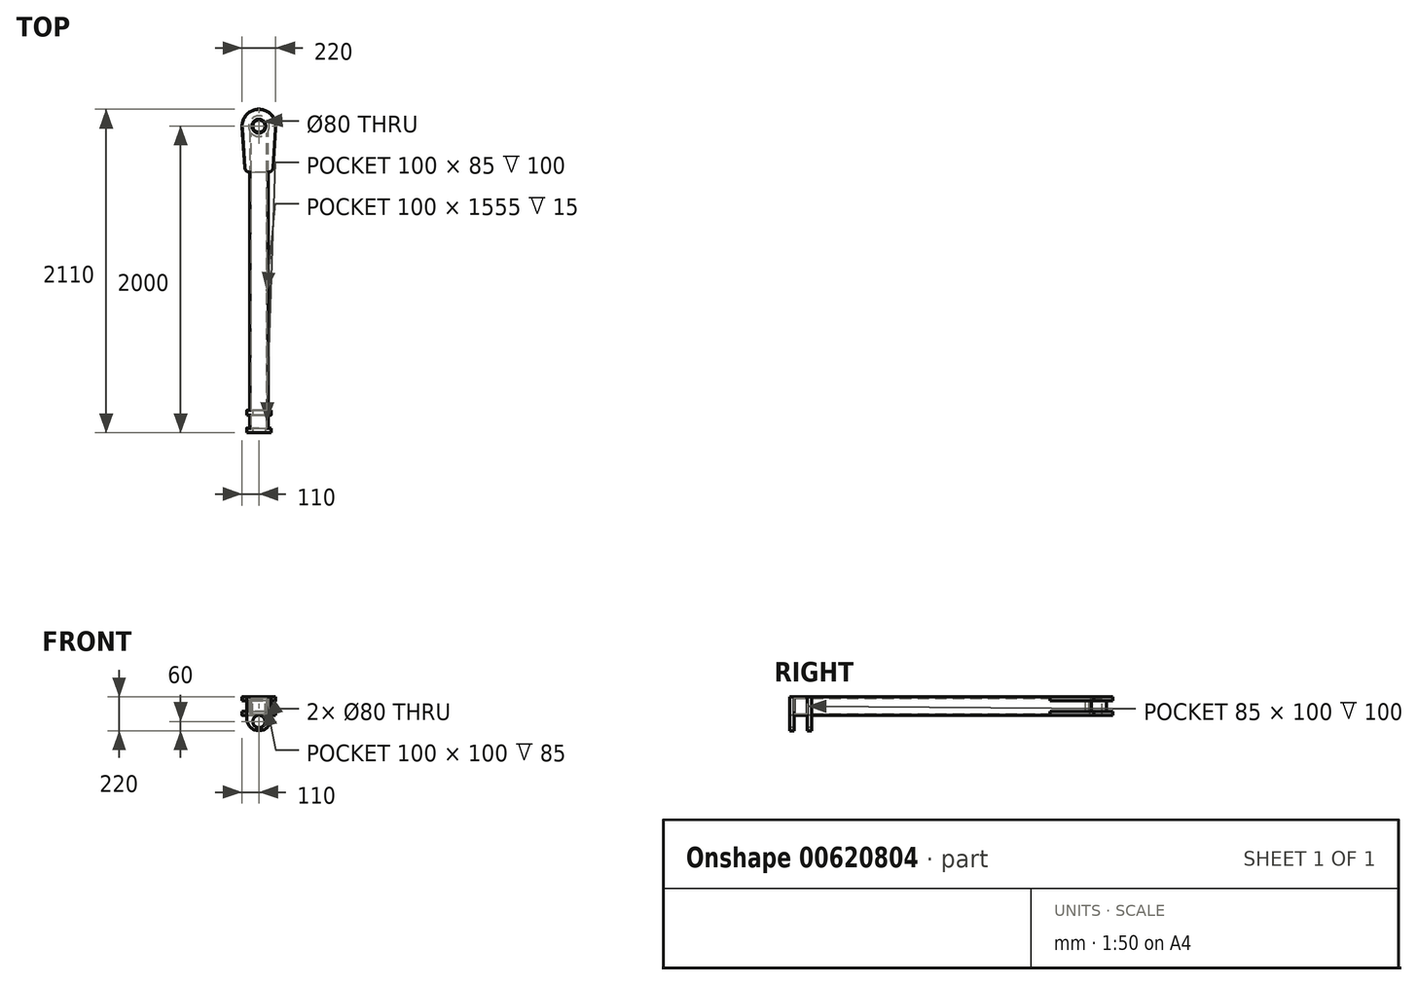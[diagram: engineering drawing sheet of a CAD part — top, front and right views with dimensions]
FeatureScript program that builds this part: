
annotation { "Feature Type Name" : "Feature", "Feature Type Description" : "" }
export const myFeature = defineFeature(function(context is Context, id is Id, definition is map)
    precondition{}
    {
        {
            var Q0;
            Q0=qCreatedBy(makeId("Front.planeOp"),FACE);
            var sketch = newSketch(context, id + "F0", { "sketchPlane" : qUnion([Q0])});
            skLineSegment(sketch, "E0.bottom", {"start": v(-60, 60) * mm, "end": v(60, 60) * mm});
            skLineSegment(sketch, "E0.top", {"start": v(-60, -60) * mm, "end": v(60, -60) * mm});
            skLineSegment(sketch, "E0.left", {"start": v(-60, 60) * mm, "end": v(-60, -60) * mm});
            skLineSegment(sketch, "E0.right", {"start": v(60, 60) * mm, "end": v(60, -60) * mm});
            skPoint(sketch, "E0.middle", {"position": v(0, 0) * mm});
            skLineSegment(sketch, "E1.bottom", {"start": v(-50, 50) * mm, "end": v(50, 50) * mm});
            skLineSegment(sketch, "E1.top", {"start": v(-50, -50) * mm, "end": v(50, -50) * mm});
            skLineSegment(sketch, "E1.left", {"start": v(-50, 50) * mm, "end": v(-50, -50) * mm});
            skLineSegment(sketch, "E1.right", {"start": v(50, 50) * mm, "end": v(50, -50) * mm});
            skSolve(sketch);
        }
        {
            var Q0;
            Q0 = qSketchRegion(id + "F0", true);
            extrude(context, id + "F1", {"entities" : qUnion([Q0]), "endBound" : BoundingType.SYMMETRIC, "depth" : 2000 * mm, "offsetDistance" : 25 * mm});
        }
        {
            var Q0;
            Q0=makeQuery(id+"F1.opExtrude","SWEPT_FACE",FACE,{"disambiguationData":[OSD([sQuery(id+"F0.wireOp",EDGE,"E0.bottom")])]});
            var sketch = newSketch(context, id + "F2", { "sketchPlane" : qUnion([Q0])});
            skCircle(sketch, "E2", {"center": v(0, 1000) * mm, "radius": 67.5 * mm});
            skSolve(sketch);
        }
        {
            var Q0;
            Q0 = qSketchRegion(id + "F2", true);
            extrude(context, id + "F3", {"entities" : qUnion([Q0]), "operationType" : NewBodyOperationType.ADD, "oppositeDirection" : true, "depth" : 120 * mm, "offsetDistance" : 25 * mm});
        }
        {
            var Q0;
            Q0=makeQuery(id+"F3.boolean.opBoolean","MERGE",FACE,{"derivedFrom":[makeQuery(id+"F1.opExtrude","SWEPT_FACE",FACE,{"disambiguationData":[OSD([sQuery(id+"F0.wireOp",EDGE,"E0.bottom")])]}),makeQuery(id+"F3.opExtrude","CAP_FACE",FACE,{"disambiguationData":[OSD([sQuery(id+"F2.wireOp",EDGE,"E2")])],"isStart":true})]});
            var sketch = newSketch(context, id + "F4", { "sketchPlane" : qUnion([Q0])});
            skCircle(sketch, "E3", {"center": v(0, 1000) * mm, "radius": 40 * mm});
            skSolve(sketch);
        }
        {
            var Q0;
            Q0 = qSketchRegion(id + "F4", true);
            extrude(context, id + "F5", {"entities" : qUnion([Q0]), "operationType" : NewBodyOperationType.REMOVE, "oppositeDirection" : true, "depth" : 120 * mm, "offsetDistance" : 25 * mm});
        }
        {
            var Q0;
            Q0=makeQuery(id+"F3.boolean.opBoolean","MERGE",FACE,{"derivedFrom":[makeQuery(id+"F1.opExtrude","SWEPT_FACE",FACE,{"disambiguationData":[OSD([sQuery(id+"F0.wireOp",EDGE,"E0.bottom")])]}),makeQuery(id+"F3.opExtrude","CAP_FACE",FACE,{"disambiguationData":[OSD([sQuery(id+"F2.wireOp",EDGE,"E2")])],"isStart":true})]});
            var sketch = newSketch(context, id + "F6", { "sketchPlane" : qUnion([Q0])});
            skCircle(sketch, "E4", {"center": v(0, 1000) * mm, "radius": 110 * mm});
            skLineSegment(sketch, "E5", {"start": v(-110, 1000) * mm, "end": v(-90, 700) * mm});
            skLineSegment(sketch, "E6", {"start": v(-90, 700) * mm, "end": v(90, 700) * mm});
            skLineSegment(sketch, "E7", {"start": v(90, 700) * mm, "end": v(110, 1000) * mm});
            skSolve(sketch);
        }
        {
            var Q0;
            Q0 = qSketchRegion(id + "F6", true);
            extrude(context, id + "F7", {"entities" : qUnion([Q0]), "operationType" : NewBodyOperationType.ADD, "oppositeDirection" : true, "depth" : 25 * mm, "offsetDistance" : 25 * mm});
        }
        {
            var Q0;
            Q0=makeQuery(id+"F3.boolean.opBoolean","MERGE",FACE,{"derivedFrom":[makeQuery(id+"F1.opExtrude","SWEPT_FACE",FACE,{"disambiguationData":[OSD([sQuery(id+"F0.wireOp",EDGE,"E0.top")])]}),makeQuery(id+"F3.opExtrude","CAP_FACE",FACE,{"disambiguationData":[OSD([sQuery(id+"F2.wireOp",EDGE,"E2")])],"isStart":false})]});
            var sketch = newSketch(context, id + "F8", { "sketchPlane" : qUnion([Q0])});
            skCircle(sketch, "E8", {"center": v(0, -1000) * mm, "radius": 110 * mm});
            skLineSegment(sketch, "E9", {"start": v(110, -1000) * mm, "end": v(90, -700) * mm});
            skLineSegment(sketch, "E10", {"start": v(90, -700) * mm, "end": v(-90, -700) * mm});
            skLineSegment(sketch, "E11", {"start": v(-90, -700) * mm, "end": v(-110.25, -1000) * mm});
            skSolve(sketch);
        }
        {
            var Q0;
            Q0 = qSketchRegion(id + "F8", true);
            extrude(context, id + "F9", {"entities" : qUnion([Q0]), "operationType" : NewBodyOperationType.ADD, "oppositeDirection" : true, "depth" : 25 * mm, "offsetDistance" : 25 * mm});
        }
        {
            var Q0;
            Q0=makeQuery(id+"F9.boolean.opBoolean","MERGE",FACE,{"derivedFrom":[makeQuery(id+"F3.boolean.opBoolean","MERGE",FACE,{"derivedFrom":[makeQuery(id+"F1.opExtrude","SWEPT_FACE",FACE,{"disambiguationData":[OSD([sQuery(id+"F0.wireOp",EDGE,"E0.top")])]}),makeQuery(id+"F3.opExtrude","CAP_FACE",FACE,{"disambiguationData":[OSD([sQuery(id+"F2.wireOp",EDGE,"E2")])],"isStart":false})]}),makeQuery(id+"F9.opExtrude","CAP_FACE",FACE,{"disambiguationData":[OSD([sQuery(id+"F8.wireOp",EDGE,"E8"),sQuery(id+"F8.wireOp",EDGE,"E9"),sQuery(id+"F8.wireOp",EDGE,"E10"),sQuery(id+"F8.wireOp",EDGE,"E11")])],"isStart":true})]});
            var sketch = newSketch(context, id + "F10", { "sketchPlane" : qUnion([Q0])});
            skCircle(sketch, "E12", {"center": v(0, -1000) * mm, "radius": 40 * mm});
            skSolve(sketch);
        }
        {
            var Q0;
            Q0 = qSketchRegion(id + "F10", true);
            extrude(context, id + "F11", {"entities" : qUnion([Q0]), "operationType" : NewBodyOperationType.REMOVE, "oppositeDirection" : true, "depth" : 160 * mm, "offsetDistance" : 25 * mm});
        }
        {
            var Q0;
            Q0=makeQuery(id+"F1.opExtrude","SWEPT_FACE",FACE,{"disambiguationData":[OSD([sQuery(id+"F0.wireOp",EDGE,"E0.right")])]});
            var sketch = newSketch(context, id + "F12", { "sketchPlane" : qUnion([Q0])});
            skLineSegment(sketch, "E13.bottom", {"start": v(-885, 60) * mm, "end": v(-855, 60) * mm});
            skLineSegment(sketch, "E13.top", {"start": v(-885, -160) * mm, "end": v(-855, -160) * mm});
            skLineSegment(sketch, "E13.left", {"start": v(-885, 60) * mm, "end": v(-885, -160) * mm});
            skLineSegment(sketch, "E13.right", {"start": v(-855, 60) * mm, "end": v(-855, -160) * mm});
            skSolve(sketch);
        }
        {
            var Q0;
            Q0 = qSketchRegion(id + "F12", true);
            extrude(context, id + "F13", {"entities" : qUnion([Q0]), "operationType" : NewBodyOperationType.ADD, "oppositeDirection" : true, "depth" : 140 * mm, "offsetDistance" : 25 * mm});
        }
        {
            var Q0;
            Q0=makeQuery(id+"F13.boolean.opBoolean","MERGE",FACE,{"derivedFrom":[makeQuery(id+"F1.opExtrude","SWEPT_FACE",FACE,{"disambiguationData":[OSD([sQuery(id+"F0.wireOp",EDGE,"E0.right")])]}),makeQuery(id+"F13.opExtrude","CAP_FACE",FACE,{"disambiguationData":[OSD([sQuery(id+"F12.wireOp",EDGE,"E13.bottom"),sQuery(id+"F12.wireOp",EDGE,"E13.top"),sQuery(id+"F12.wireOp",EDGE,"E13.left"),sQuery(id+"F12.wireOp",EDGE,"E13.right")])],"isStart":true})]});
            var sketch = newSketch(context, id + "F14", { "sketchPlane" : qUnion([Q0])});
            skLineSegment(sketch, "E14.bottom", {"start": v(-885, -160) * mm, "end": v(-855, -160) * mm});
            skLineSegment(sketch, "E14.top", {"start": v(-885, 60) * mm, "end": v(-855, 60) * mm});
            skLineSegment(sketch, "E14.left", {"start": v(-885, -160) * mm, "end": v(-885, 60) * mm});
            skLineSegment(sketch, "E14.right", {"start": v(-855, -160) * mm, "end": v(-855, 60) * mm});
            skSolve(sketch);
        }
        {
            var Q0;
            Q0 = qSketchRegion(id + "F14", true);
            extrude(context, id + "F15", {"entities" : qUnion([Q0]), "operationType" : NewBodyOperationType.ADD, "depth" : 20 * mm, "offsetDistance" : 25 * mm});
        }
        {
            var Q0;
            {var subQ0=sQuery(id+"F12.wireOp",EDGE,"E13.left");var subQ1=sQuery(id+"F12.wireOp",EDGE,"E13.bottom");var subQ5=sQuery(id+"F0.wireOp",EDGE,"E0.right");Q0=makeQuery(id+"F15.boolean.opBoolean","SPLIT",FACE,{"disambiguationData":[TD([makeQuery(id+"F13.opExtrude","SWEPT_FACE",FACE,{"disambiguationData":[OSD([subQ0])]})])],"derivedFrom":makeQuery(id+"F13.boolean.opBoolean","MERGE",FACE,{"derivedFrom":[makeQuery(id+"F1.opExtrude","SWEPT_FACE",FACE,{"disambiguationData":[OSD([subQ5])]}),makeQuery(id+"F13.opExtrude","CAP_FACE",FACE,{"disambiguationData":[OSD([subQ1,sQuery(id+"F12.wireOp",EDGE,"E13.top"),subQ0,sQuery(id+"F12.wireOp",EDGE,"E13.right")])],"isStart":true})]})});}
            var sketch = newSketch(context, id + "F16", { "sketchPlane" : qUnion([Q0])});
            skLineSegment(sketch, "E15.bottom", {"start": v(-1000, 60) * mm, "end": v(-970, 60) * mm});
            skLineSegment(sketch, "E15.top", {"start": v(-1000, -160) * mm, "end": v(-970, -160) * mm});
            skLineSegment(sketch, "E15.left", {"start": v(-1000, 60) * mm, "end": v(-1000, -160) * mm});
            skLineSegment(sketch, "E15.right", {"start": v(-970, 60) * mm, "end": v(-970, -160) * mm});
            skSolve(sketch);
        }
        {
            var Q0;
            Q0 = qSketchRegion(id + "F16", true);
            extrude(context, id + "F17", {"entities" : qUnion([Q0]), "operationType" : NewBodyOperationType.ADD, "oppositeDirection" : true, "depth" : 140 * mm, "offsetDistance" : 25 * mm});
        }
        {
            var Q0;
            {var subQ0=sQuery(id+"F12.wireOp",EDGE,"E13.left");var subQ1=sQuery(id+"F12.wireOp",EDGE,"E13.bottom");var subQ5=sQuery(id+"F0.wireOp",EDGE,"E0.right");Q0=makeQuery(id+"F17.boolean.opBoolean","MERGE",FACE,{"derivedFrom":[makeQuery(id+"F15.boolean.opBoolean","SPLIT",FACE,{"disambiguationData":[TD([makeQuery(id+"F13.opExtrude","SWEPT_FACE",FACE,{"disambiguationData":[OSD([subQ0])]})])],"derivedFrom":makeQuery(id+"F13.boolean.opBoolean","MERGE",FACE,{"derivedFrom":[makeQuery(id+"F1.opExtrude","SWEPT_FACE",FACE,{"disambiguationData":[OSD([subQ5])]}),makeQuery(id+"F13.opExtrude","CAP_FACE",FACE,{"disambiguationData":[OSD([subQ1,sQuery(id+"F12.wireOp",EDGE,"E13.top"),subQ0,sQuery(id+"F12.wireOp",EDGE,"E13.right")])],"isStart":true})]})}),makeQuery(id+"F17.opExtrude","CAP_FACE",FACE,{"disambiguationData":[OSD([sQuery(id+"F16.wireOp",EDGE,"E15.bottom"),sQuery(id+"F16.wireOp",EDGE,"E15.top"),sQuery(id+"F16.wireOp",EDGE,"E15.left"),sQuery(id+"F16.wireOp",EDGE,"E15.right")])],"isStart":true})]});}
            var sketch = newSketch(context, id + "F18", { "sketchPlane" : qUnion([Q0])});
            skLineSegment(sketch, "E16.bottom", {"start": v(-1000, -160) * mm, "end": v(-970, -160) * mm});
            skLineSegment(sketch, "E16.top", {"start": v(-1000, 60) * mm, "end": v(-970, 60) * mm});
            skLineSegment(sketch, "E16.left", {"start": v(-1000, -160) * mm, "end": v(-1000, 60) * mm});
            skLineSegment(sketch, "E16.right", {"start": v(-970, -160) * mm, "end": v(-970, 60) * mm});
            skSolve(sketch);
        }
        {
            var Q0;
            Q0 = qSketchRegion(id + "F18", true);
            extrude(context, id + "F19", {"entities" : qUnion([Q0]), "operationType" : NewBodyOperationType.ADD, "depth" : 20 * mm, "offsetDistance" : 25 * mm});
        }
        {
            var Q0;
            Q0=makeQuery(id+"F19.boolean.opBoolean","MERGE",FACE,{"derivedFrom":[makeQuery(id+"F17.boolean.opBoolean","MERGE",FACE,{"derivedFrom":[makeQuery(id+"F1.opExtrude","CAP_FACE",FACE,{"disambiguationData":[OSD([sQuery(id+"F0.wireOp",EDGE,"E0.bottom"),sQuery(id+"F0.wireOp",EDGE,"E0.top"),sQuery(id+"F0.wireOp",EDGE,"E0.left"),sQuery(id+"F0.wireOp",EDGE,"E0.right"),sQuery(id+"F0.wireOp",EDGE,"E1.bottom"),sQuery(id+"F0.wireOp",EDGE,"E1.top"),sQuery(id+"F0.wireOp",EDGE,"E1.left"),sQuery(id+"F0.wireOp",EDGE,"E1.right")])],"isStart":false}),makeQuery(id+"F17.opExtrude","SWEPT_FACE",FACE,{"disambiguationData":[OSD([sQuery(id+"F16.wireOp",EDGE,"E15.left")])]})]}),makeQuery(id+"F19.opExtrude","SWEPT_FACE",FACE,{"disambiguationData":[OSD([sQuery(id+"F18.wireOp",EDGE,"E16.left")])]})]});
            var sketch = newSketch(context, id + "F20", { "sketchPlane" : qUnion([Q0])});
            skCircle(sketch, "E17", {"center": v(0, -100) * mm, "radius": 40 * mm});
            skPoint(sketch, "E17.centerSnap0", {"position": v(0, -160) * mm});
            skSolve(sketch);
        }
        {
            var Q0;
            Q0 = qSketchRegion(id + "F20", true);
            extrude(context, id + "F21", {"entities" : qUnion([Q0]), "operationType" : NewBodyOperationType.REMOVE, "oppositeDirection" : true, "depth" : 145 * mm, "offsetDistance" : 25 * mm});
        }
        {
            var Q0;
            {var subQ0=sQuery(id+"F6.wireOp",EDGE,"E6");var subQ1=sQuery(id+"F0.wireOp",EDGE,"E0.right");var subQ4=sQuery(id+"F0.wireOp",EDGE,"E0.bottom");Q0=makeQuery(id+"F15.boolean.opBoolean","SPLIT",EDGE,{"disambiguationData":[TD([makeQuery(id+"F7.opExtrude","SWEPT_FACE",FACE,{"disambiguationData":[OSD([subQ0])]})])],"derivedFrom":makeQuery(id+"F1.opExtrude","SWEPT_EDGE",EDGE,{"disambiguationData":[OSD([subQ4,subQ1])]})});}
            var Q1;
            {var subQ0=sQuery(id+"F8.wireOp",EDGE,"E10");var subQ1=sQuery(id+"F0.wireOp",EDGE,"E0.top");var subQ2=sQuery(id+"F0.wireOp",EDGE,"E0.right");Q1=makeQuery(id+"F13.boolean.opBoolean","SPLIT",EDGE,{"disambiguationData":[TD([makeQuery(id+"F9.opExtrude","SWEPT_FACE",FACE,{"disambiguationData":[OSD([subQ0])]})])],"derivedFrom":makeQuery(id+"F1.opExtrude","SWEPT_EDGE",EDGE,{"disambiguationData":[OSD([subQ1,subQ2])]})});}
            var Q2;
            {var subQ0=sQuery(id+"F0.wireOp",EDGE,"E0.top");var subQ1=sQuery(id+"F0.wireOp",EDGE,"E0.right");var subQ2=sQuery(id+"F12.wireOp",EDGE,"E13.left");Q2=makeQuery(id+"F13.boolean.opBoolean","SPLIT",EDGE,{"disambiguationData":[TD([makeQuery(id+"F13.opExtrude","SWEPT_FACE",FACE,{"disambiguationData":[OSD([subQ2])]})])],"derivedFrom":makeQuery(id+"F1.opExtrude","SWEPT_EDGE",EDGE,{"disambiguationData":[OSD([subQ0,subQ1])]})});}
            var Q3;
            {var subQ0=sQuery(id+"F0.wireOp",EDGE,"E0.right");var subQ1=sQuery(id+"F0.wireOp",EDGE,"E0.bottom");var subQ2=sQuery(id+"F12.wireOp",EDGE,"E13.left");Q3=makeQuery(id+"F15.boolean.opBoolean","SPLIT",EDGE,{"disambiguationData":[TD([makeQuery(id+"F13.opExtrude","SWEPT_FACE",FACE,{"disambiguationData":[OSD([subQ2])]})])],"derivedFrom":makeQuery(id+"F1.opExtrude","SWEPT_EDGE",EDGE,{"disambiguationData":[OSD([subQ1,subQ0])]})});}
            var Q4;
            {var subQ0=sQuery(id+"F6.wireOp",EDGE,"E6");var subQ1=sQuery(id+"F0.wireOp",EDGE,"E0.left");var subQ2=sQuery(id+"F0.wireOp",EDGE,"E0.bottom");Q4=makeQuery(id+"F13.boolean.opBoolean","SPLIT",EDGE,{"disambiguationData":[TD([makeQuery(id+"F7.opExtrude","SWEPT_FACE",FACE,{"disambiguationData":[OSD([subQ0])]})])],"derivedFrom":makeQuery(id+"F1.opExtrude","SWEPT_EDGE",EDGE,{"disambiguationData":[OSD([subQ2,subQ1])]})});}
            var Q5;
            {var subQ0=sQuery(id+"F0.wireOp",EDGE,"E0.left");var subQ1=sQuery(id+"F0.wireOp",EDGE,"E0.bottom");Q5=makeQuery(id+"F13.boolean.opBoolean","SPLIT",EDGE,{"disambiguationData":[TD([makeQuery(id+"F13.opExtrude","SWEPT_FACE",FACE,{"disambiguationData":[OSD([sQuery(id+"F12.wireOp",EDGE,"E13.left")])]})])],"derivedFrom":makeQuery(id+"F1.opExtrude","SWEPT_EDGE",EDGE,{"disambiguationData":[OSD([subQ1,subQ0])]})});}
            var Q6;
            {var subQ0=sQuery(id+"F0.wireOp",EDGE,"E0.top");var subQ1=sQuery(id+"F0.wireOp",EDGE,"E0.left");Q6=makeQuery(id+"F13.boolean.opBoolean","SPLIT",EDGE,{"disambiguationData":[TD([makeQuery(id+"F13.opExtrude","SWEPT_FACE",FACE,{"disambiguationData":[OSD([sQuery(id+"F12.wireOp",EDGE,"E13.left")])]})])],"derivedFrom":makeQuery(id+"F1.opExtrude","SWEPT_EDGE",EDGE,{"disambiguationData":[OSD([subQ0,subQ1])]})});}
            var Q7;
            {var subQ0=sQuery(id+"F8.wireOp",EDGE,"E10");var subQ1=sQuery(id+"F0.wireOp",EDGE,"E0.top");var subQ2=sQuery(id+"F0.wireOp",EDGE,"E0.left");Q7=makeQuery(id+"F13.boolean.opBoolean","SPLIT",EDGE,{"disambiguationData":[TD([makeQuery(id+"F9.opExtrude","SWEPT_FACE",FACE,{"disambiguationData":[OSD([subQ0])]})])],"derivedFrom":makeQuery(id+"F1.opExtrude","SWEPT_EDGE",EDGE,{"disambiguationData":[OSD([subQ1,subQ2])]})});}
            fillet(context, id + "F22", {"entities" : qUnion([Q0, Q1, Q2, Q3, Q4, Q5, Q6, Q7]), "radius" : 10 * mm, "tangentPropagation" : true, "allowEdgeOverflow" : false});
        }
        {
            var Q0;
            Q0=makeQuery(id+"F17.opExtrude","CAP_EDGE",EDGE,{"disambiguationData":[OSD([sQuery(id+"F16.wireOp",EDGE,"E15.top")])],"isStart":false});
            var Q1;
            Q1=makeQuery(id+"F19.opExtrude","CAP_EDGE",EDGE,{"disambiguationData":[OSD([sQuery(id+"F18.wireOp",EDGE,"E16.bottom")])],"isStart":false});
            var Q2;
            Q2=makeQuery(id+"F15.opExtrude","CAP_EDGE",EDGE,{"disambiguationData":[OSD([sQuery(id+"F14.wireOp",EDGE,"E14.bottom")])],"isStart":false});
            var Q3;
            Q3=makeQuery(id+"F13.opExtrude","CAP_EDGE",EDGE,{"disambiguationData":[OSD([sQuery(id+"F12.wireOp",EDGE,"E13.top")])],"isStart":false});
            fillet(context, id + "F23", {"entities" : qUnion([Q0, Q1, Q2, Q3]), "radius" : 80 * mm, "tangentPropagation" : true, "allowEdgeOverflow" : false});
        }
        {
            var Q0;
            Q0=makeQuery(id+"F9.opExtrude","SWEPT_EDGE",EDGE,{"disambiguationData":[OSD([sQuery(id+"F8.wireOp",EDGE,"E10"),sQuery(id+"F8.wireOp",EDGE,"E11")])]});
            var Q1;
            Q1=makeQuery(id+"F7.opExtrude","SWEPT_EDGE",EDGE,{"disambiguationData":[OSD([sQuery(id+"F6.wireOp",EDGE,"E5"),sQuery(id+"F6.wireOp",EDGE,"E6")])]});
            var Q2;
            Q2=makeQuery(id+"F9.opExtrude","SWEPT_EDGE",EDGE,{"disambiguationData":[OSD([sQuery(id+"F8.wireOp",EDGE,"E9"),sQuery(id+"F8.wireOp",EDGE,"E10")])]});
            var Q3;
            Q3=makeQuery(id+"F7.opExtrude","SWEPT_EDGE",EDGE,{"disambiguationData":[OSD([sQuery(id+"F6.wireOp",EDGE,"E6"),sQuery(id+"F6.wireOp",EDGE,"E7")])]});
            fillet(context, id + "F24", {"entities" : qUnion([Q0, Q1, Q2, Q3]), "radius" : 30 * mm, "tangentPropagation" : true, "allowEdgeOverflow" : false});
        }
        {
            var Q0;
            Q0=makeQuery(id+"F11.boolean.opBoolean","INTERSECT",EDGE,{"derivedFrom":[makeQuery(id+"F7.boolean.opBoolean","MERGE",FACE,{"derivedFrom":[makeQuery(id+"F3.boolean.opBoolean","MERGE",FACE,{"derivedFrom":[makeQuery(id+"F1.opExtrude","SWEPT_FACE",FACE,{"disambiguationData":[OSD([sQuery(id+"F0.wireOp",EDGE,"E0.bottom")])]}),makeQuery(id+"F3.opExtrude","CAP_FACE",FACE,{"disambiguationData":[OSD([sQuery(id+"F2.wireOp",EDGE,"E2")])],"isStart":true})]}),makeQuery(id+"F7.opExtrude","CAP_FACE",FACE,{"disambiguationData":[OSD([sQuery(id+"F6.wireOp",EDGE,"E4"),sQuery(id+"F6.wireOp",EDGE,"E5"),sQuery(id+"F6.wireOp",EDGE,"E6"),sQuery(id+"F6.wireOp",EDGE,"E7")])],"isStart":true})]}),makeQuery(id+"F11.opExtrude","SWEPT_FACE",FACE,{"disambiguationData":[OSD([sQuery(id+"F10.wireOp",EDGE,"E12")])]})]});
            var Q1;
            Q1=makeQuery(id+"F11.boolean.opBoolean","COPY",EDGE,{"derivedFrom":makeQuery(id+"F11.opExtrude","CAP_EDGE",EDGE,{"disambiguationData":[OSD([sQuery(id+"F10.wireOp",EDGE,"E12")])],"isStart":true})});
            chamfer(context, id + "F25", {"entities" : qUnion([Q0, Q1]), "width" : 5 * mm, "tangentPropagation" : true});
        }
    });
